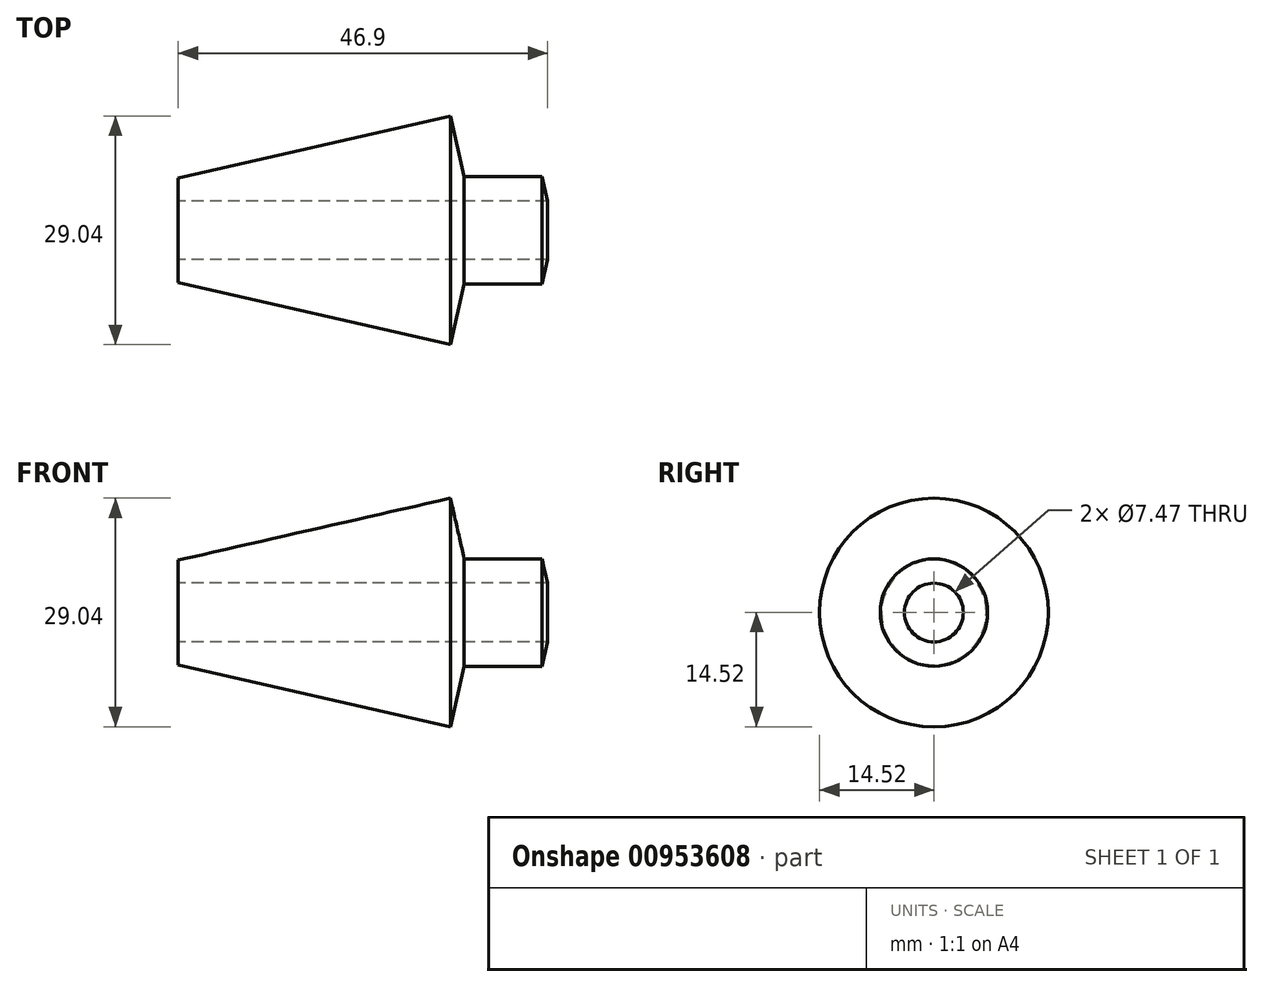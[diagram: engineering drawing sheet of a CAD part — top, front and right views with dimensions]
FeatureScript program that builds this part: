
annotation { "Feature Type Name" : "Feature", "Feature Type Description" : "" }
export const myFeature = defineFeature(function(context is Context, id is Id, definition is map)
    precondition{}
    {
        {
            var Q0;
            Q0=qCreatedBy(makeId("Front.planeOp"),FACE);
            var sketch = newSketch(context, id + "F0", { "sketchPlane" : qUnion([Q0])});
            skLineSegment(sketch, "E0", {"start": v(-20.1, 6.65) * mm, "end": v(14.46, 14.52) * mm});
            skLineSegment(sketch, "E1", {"start": v(14.46, 14.52) * mm, "end": v(16.22, 6.82) * mm});
            skLineSegment(sketch, "E2", {"start": v(16.22, 6.82) * mm, "end": v(26.1, 6.82) * mm});
            skPoint(sketch, "E3.end.orphan", {"position": v(26.1, 0) * mm});
            skLineSegment(sketch, "E4", {"start": v(26.1, 6.82) * mm, "end": v(26.8, 3.73) * mm});
            skLineSegment(sketch, "E5", {"start": v(26.8, 3.73) * mm, "end": v(-20.1, 3.73) * mm});
            skLineSegment(sketch, "E6", {"start": v(-20.1, 3.73) * mm, "end": v(-20.1, 6.65) * mm});
            skLineSegment(sketch, "E7", {"start": v(-32.77, 0) * mm, "end": v(36.71, 0) * mm});
            skSolve(sketch);
        }
        {
            var Q0;
            Q0 = qSketchRegion(id + "F0", true);
            var Q1;
            Q1=sQuery(id+"F0.wireOp",EDGE,"E7");
            revolve(context, id + "F1", {"surfaceOperationType" : NewSurfaceOperationType.NEW, "entities" : qUnion([Q0]), "axis" : qUnion([Q1]), "revolveType" : RevolveType.FULL});
        }
    });
